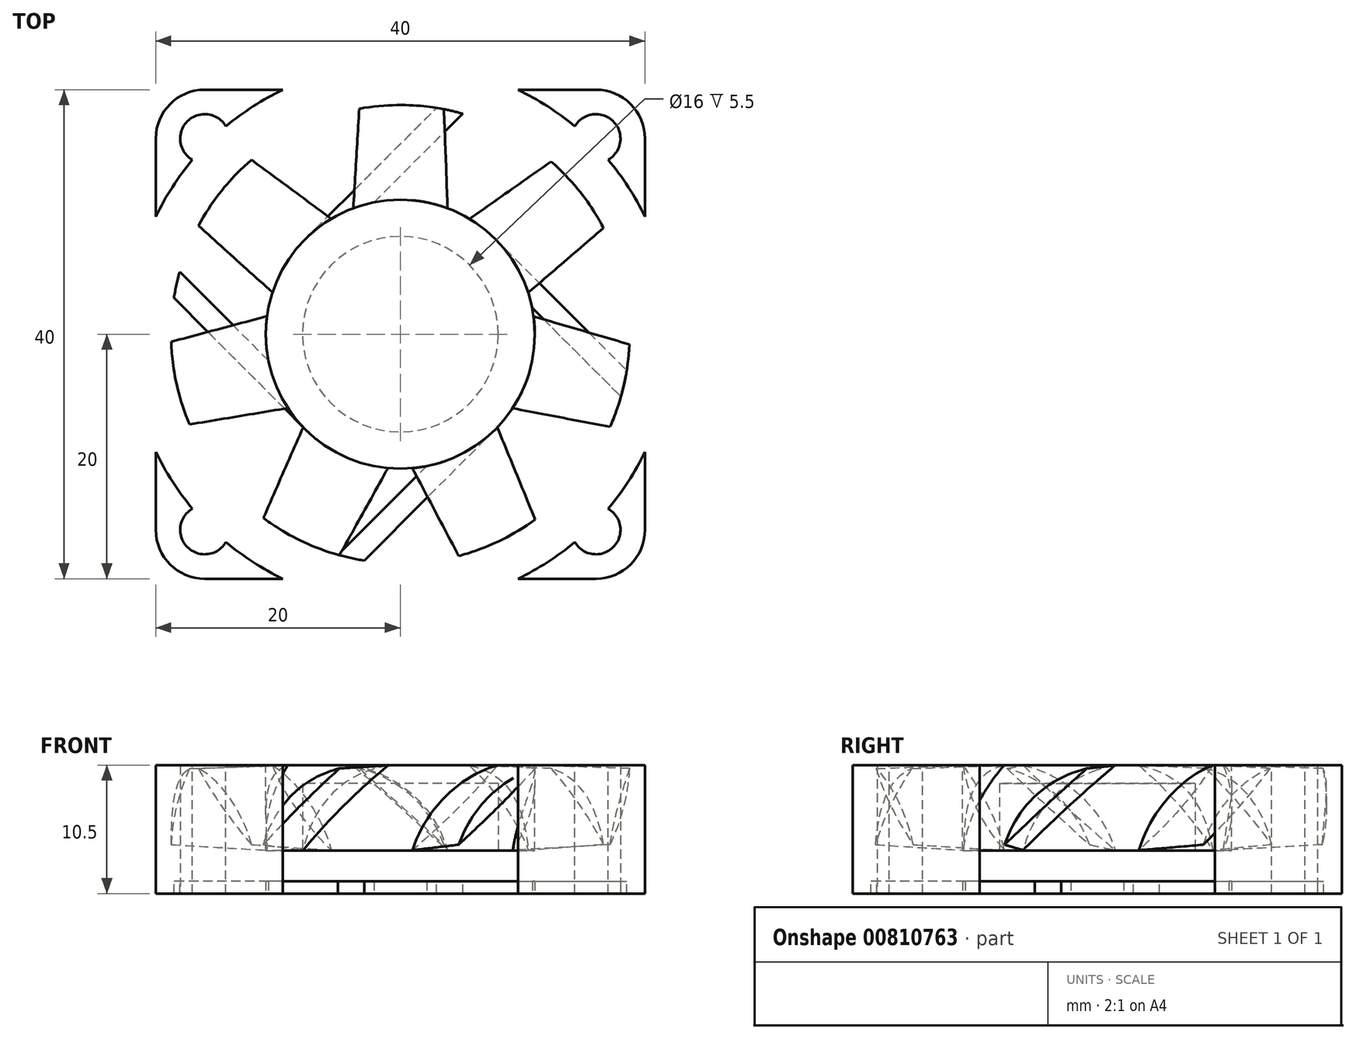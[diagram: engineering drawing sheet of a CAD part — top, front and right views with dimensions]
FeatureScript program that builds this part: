
annotation { "Feature Type Name" : "Feature", "Feature Type Description" : "" }
export const myFeature = defineFeature(function(context is Context, id is Id, definition is map)
    precondition{}
    {
        {
            var Q0;
            Q0=qCreatedBy(makeId("Top.planeOp"),FACE);
            var sketch = newSketch(context, id + "F0", { "sketchPlane" : qUnion([Q0])});
            skLineSegment(sketch, "E0.bottom", {"start": v(16, 20) * mm, "end": v(-16, 20) * mm});
            skLineSegment(sketch, "E0.top", {"start": v(16, -20) * mm, "end": v(-16, -20) * mm});
            skLineSegment(sketch, "E0.left", {"start": v(20, 16) * mm, "end": v(20, -16) * mm});
            skLineSegment(sketch, "E0.right", {"start": v(-20, 16) * mm, "end": v(-20, -16) * mm});
            skPoint(sketch, "E0.middle", {"position": v(0, 0) * mm});
            skPoint(sketch, "E1.visualSharp", {"position": v(20, 20) * mm});
            skArc(sketch, "E1.filletArc", {"start": v(20, 16) * mm, "mid": v(18.83, 18.83) * mm, "end": v(16, 20) * mm});
            skPoint(sketch, "E2.visualSharp", {"position": v(-20, 20) * mm});
            skArc(sketch, "E2.filletArc", {"start": v(-16, 20) * mm, "mid": v(-18.83, 18.83) * mm, "end": v(-20, 16) * mm});
            skPoint(sketch, "E3.visualSharp", {"position": v(-20, -20) * mm});
            skArc(sketch, "E3.filletArc", {"start": v(-20, -16) * mm, "mid": v(-18.83, -18.83) * mm, "end": v(-16, -20) * mm});
            skPoint(sketch, "E4.visualSharp", {"position": v(20, -20) * mm});
            skArc(sketch, "E4.filletArc", {"start": v(16, -20) * mm, "mid": v(18.83, -18.83) * mm, "end": v(20, -16) * mm});
            skLineSegment(sketch, "E5.bottom", {"start": v(-16, 16) * mm, "end": v(16, 16) * mm, "construction": true});
            skLineSegment(sketch, "E5.top", {"start": v(-16, -16) * mm, "end": v(16, -16) * mm, "construction": true});
            skLineSegment(sketch, "E5.left", {"start": v(-16, 16) * mm, "end": v(-16, -16) * mm, "construction": true});
            skLineSegment(sketch, "E5.right", {"start": v(16, 16) * mm, "end": v(16, -16) * mm, "construction": true});
            skCircle(sketch, "E6", {"center": v(-16, 16) * mm, "radius": 2 * mm});
            skCircle(sketch, "E7", {"center": v(16, 16) * mm, "radius": 2 * mm});
            skCircle(sketch, "E8", {"center": v(16, -16) * mm, "radius": 2 * mm});
            skCircle(sketch, "E9", {"center": v(-16, -16) * mm, "radius": 2 * mm});
            skSolve(sketch);
        }
        {
            var Q0;
            Q0=makeQuery(id+"F0.imprint","IMPRINT",FACE,{"disambiguationData":[TD([[makeQuery(id+"F0.imprint","IMPRINT",EDGE,{"derivedFrom":sQuery(id+"F0.wireOp",EDGE,"E0.bottom")}),1.0]])]});
            extrude(context, id + "F1", {"entities" : qUnion([Q0]), "depth" : 10.5 * mm});
        }
        {
            var Q0;
            Q0=qCreatedBy(makeId("Top.planeOp"),FACE);
            var sketch = newSketch(context, id + "F2", { "sketchPlane" : qUnion([Q0])});
            skCircle(sketch, "E10", {"center": v(0, 0) * mm, "radius": 19.25 * mm});
            skSolve(sketch);
        }
        {
            var Q0;
            Q0=qSketchRegion(id+"F2",true);
            extrude(context, id + "F3", {"entities" : qUnion([Q0]), "operationType" : NewBodyOperationType.REMOVE, "endBound" : BoundingType.THROUGH_ALL, "depth" : 25 * mm});
        }
        {
            var Q0;
            Q0=qCreatedBy(makeId("Top.planeOp"),FACE);
            var sketch = newSketch(context, id + "F4", { "sketchPlane" : qUnion([Q0])});
            skArc(sketch, "E11", {"start": v(-7.78, -7.78) * mm, "mid": v(-3.19, -10.53) * mm, "end": v(2.15, -10.79) * mm});
            skLineSegment(sketch, "E12", {"start": v(-7.78, -7.78) * mm, "end": v(-20, 4.44) * mm});
            skLineSegment(sketch, "E13.0", {"start": v(-10.79, -2.15) * mm, "end": v(-20, 7.06) * mm});
            skLineSegment(sketch, "E14.1.0", {"start": v(2.15, -10.79) * mm, "end": v(-7.06, -20) * mm});
            skLineSegment(sketch, "E14.1.1", {"start": v(7.78, -7.78) * mm, "end": v(-4.44, -20) * mm});
            skLineSegment(sketch, "E14.2.0", {"start": v(10.79, 2.15) * mm, "end": v(20, -7.06) * mm});
            skLineSegment(sketch, "E14.2.1", {"start": v(7.78, 7.78) * mm, "end": v(20, -4.44) * mm});
            skLineSegment(sketch, "E14.3.0", {"start": v(-2.15, 10.79) * mm, "end": v(7.06, 20) * mm});
            skLineSegment(sketch, "E14.3.1", {"start": v(-7.78, 7.78) * mm, "end": v(4.44, 20) * mm});
            skArc(sketch, "E15.trimOffspring", {"start": v(-7.78, 7.78) * mm, "mid": v(-10.53, 3.19) * mm, "end": v(-10.79, -2.15) * mm});
            skArc(sketch, "E16.trimOffspring", {"start": v(7.78, 7.78) * mm, "mid": v(3.19, 10.53) * mm, "end": v(-2.15, 10.79) * mm});
            skArc(sketch, "E17.trimOffspring", {"start": v(7.78, -7.78) * mm, "mid": v(10.53, -3.19) * mm, "end": v(10.79, 2.15) * mm});
            skLineSegment(sketch, "E18", {"start": v(7.06, 20) * mm, "end": v(4.44, 20) * mm});
            skLineSegment(sketch, "E19", {"start": v(-20, 7.06) * mm, "end": v(-20, 4.44) * mm});
            skLineSegment(sketch, "E20", {"start": v(-7.06, -20) * mm, "end": v(-4.44, -20) * mm});
            skLineSegment(sketch, "E21", {"start": v(20, -7.06) * mm, "end": v(20, -4.44) * mm});
            skSolve(sketch);
        }
        {
            var Q0;
            Q0=qSketchRegion(id+"F4",true);
            extrude(context, id + "F5", {"entities" : qUnion([Q0]), "operationType" : NewBodyOperationType.ADD, "depth" : 1 * mm});
        }
        {
            var Q0;
            Q0=makeQuery(id+"F1.opExtrude","CAP_FACE",FACE,{"disambiguationData":[OSD([sQuery(id+"F0.wireOp",EDGE,"E0.bottom"),sQuery(id+"F0.wireOp",EDGE,"E0.top"),sQuery(id+"F0.wireOp",EDGE,"E0.left"),sQuery(id+"F0.wireOp",EDGE,"E0.right"),sQuery(id+"F0.wireOp",EDGE,"E1.filletArc"),sQuery(id+"F0.wireOp",EDGE,"E2.filletArc"),sQuery(id+"F0.wireOp",EDGE,"E3.filletArc"),sQuery(id+"F0.wireOp",EDGE,"E4.filletArc"),sQuery(id+"F0.wireOp",EDGE,"E6"),sQuery(id+"F0.wireOp",EDGE,"E7"),sQuery(id+"F0.wireOp",EDGE,"E8"),sQuery(id+"F0.wireOp",EDGE,"E9")])],"isStart":false});
            var sketch = newSketch(context, id + "F6", { "sketchPlane" : qUnion([Q0])});
            skCircle(sketch, "E22", {"center": v(0, 0) * mm, "radius": 11 * mm});
            skSolve(sketch);
        }
        {
            var Q0;
            Q0=qSketchRegion(id+"F6",true);
            extrude(context, id + "F7", {"entities" : qUnion([Q0]), "oppositeDirection" : true, "depth" : 7 * mm});
        }
        {
            var Q0;
            Q0=qCreatedBy(makeId("Front.planeOp"),FACE);
            cPlane(context, id + "F8", {"entities" : qUnion([Q0]), "cplaneType" : CPlaneType.OFFSET, "offset" : 9.5 * mm, "oppositeDirection" : true, "width" : 150 * mm, "height" : 150 * mm});
        }
        {
            var Q0;
            Q0=qCreatedBy(id+"F8.planeOp",FACE);
            var sketch = newSketch(context, id + "F9", { "sketchPlane" : qUnion([Q0])});
            skLineSegment(sketch, "E23", {"start": v(0, 0) * mm, "end": v(0, 7) * mm, "construction": true});
            skPoint(sketch, "E24", {"position": v(0, 3.5) * mm});
            skLineSegment(sketch, "E25", {"start": v(3.89, 3.5) * mm, "end": v(-3.89, 10.5) * mm});
            skArc(sketch, "E26", {"start": v(3.89, 3.5) * mm, "mid": v(1, 8.11) * mm, "end": v(-3.89, 10.5) * mm});
            skSolve(sketch);
        }
        {
            var Q0;
            Q0=qSketchRegion(id+"F9",true);
            extrude(context, id + "F10", {"entities" : qUnion([Q0]), "oppositeDirection" : true, "depth" : 10 * mm, "hasDraft" : true, "draftAngle" : 1 * degree, "draftPullDirection" : true});
        }
        {
            var Q0;
            Q0=makeQuery(id+"F10.opExtrude","SWEPT_BODY",BODY,{"disambiguationData":[OSD([sQuery(id+"F9.wireOp",EDGE,"E25"),sQuery(id+"F9.wireOp",EDGE,"E26")])]});
            var Q1;
            Q1=makeQuery(id+"F7.opExtrude","SWEPT_FACE",FACE,{"disambiguationData":[OSD([sQuery(id+"F6.wireOp",EDGE,"E22")])]});
            circularPattern(context, id + "F11", {"operationType" : NewBodyOperationType.ADD, "entities" : qUnion([Q0]), "axis" : qUnion([Q1]), "angle" : 360 * degree, "instanceCount" : 7, "equalSpace" : true});
        }
        {
            var Q0;
            Q0=makeQuery(id+"F7.opExtrude","CAP_FACE",FACE,{"disambiguationData":[OSD([sQuery(id+"F6.wireOp",EDGE,"E22")])],"isStart":true});
            var sketch = newSketch(context, id + "F12", { "sketchPlane" : qUnion([Q0])});
            skCircle(sketch, "E27", {"center": v(0, 0) * mm, "radius": 18.75 * mm});
            skCircle(sketch, "E28", {"center": v(0, 0) * mm, "radius": 22.2 * mm});
            skSolve(sketch);
        }
        {
            var Q0;
            Q0=qSketchRegion(id+"F12",true);
            extrude(context, id + "F13", {"entities" : qUnion([Q0]), "operationType" : NewBodyOperationType.REMOVE, "endBound" : BoundingType.THROUGH_ALL, "oppositeDirection" : true, "depth" : 25 * mm});
        }
        {
            var Q0;
            Q0=makeQuery(id+"F5.opExtrude","CAP_FACE",FACE,{"disambiguationData":[OSD([sQuery(id+"F4.wireOp",EDGE,"E11"),sQuery(id+"F4.wireOp",EDGE,"E12"),sQuery(id+"F4.wireOp",EDGE,"E13.0"),sQuery(id+"F4.wireOp",EDGE,"E14.1.0"),sQuery(id+"F4.wireOp",EDGE,"E14.1.1"),sQuery(id+"F4.wireOp",EDGE,"E14.2.0"),sQuery(id+"F4.wireOp",EDGE,"E14.2.1"),sQuery(id+"F4.wireOp",EDGE,"E14.3.0"),sQuery(id+"F4.wireOp",EDGE,"E14.3.1"),sQuery(id+"F4.wireOp",EDGE,"E15.trimOffspring"),sQuery(id+"F4.wireOp",EDGE,"E16.trimOffspring"),sQuery(id+"F4.wireOp",EDGE,"E17.trimOffspring"),sQuery(id+"F4.wireOp",EDGE,"E18"),sQuery(id+"F4.wireOp",EDGE,"E19"),sQuery(id+"F4.wireOp",EDGE,"E20"),sQuery(id+"F4.wireOp",EDGE,"E21")])],"isStart":false});
            var sketch = newSketch(context, id + "F14", { "sketchPlane" : qUnion([Q0])});
            skCircle(sketch, "E29", {"center": v(0, 0) * mm, "radius": 8 * mm});
            skSolve(sketch);
        }
        {
            var Q0;
            Q0=qSketchRegion(id+"F14",true);
            extrude(context, id + "F15", {"entities" : qUnion([Q0]), "operationType" : NewBodyOperationType.ADD, "depth" : 8 * mm});
        }
        {
            var Q0;
            Q0=qSketchRegion(id+"F14",true);
            extrude(context, id + "F16", {"entities" : qUnion([Q0]), "operationType" : NewBodyOperationType.REMOVE, "depth" : 8 * mm});
        }
    });
